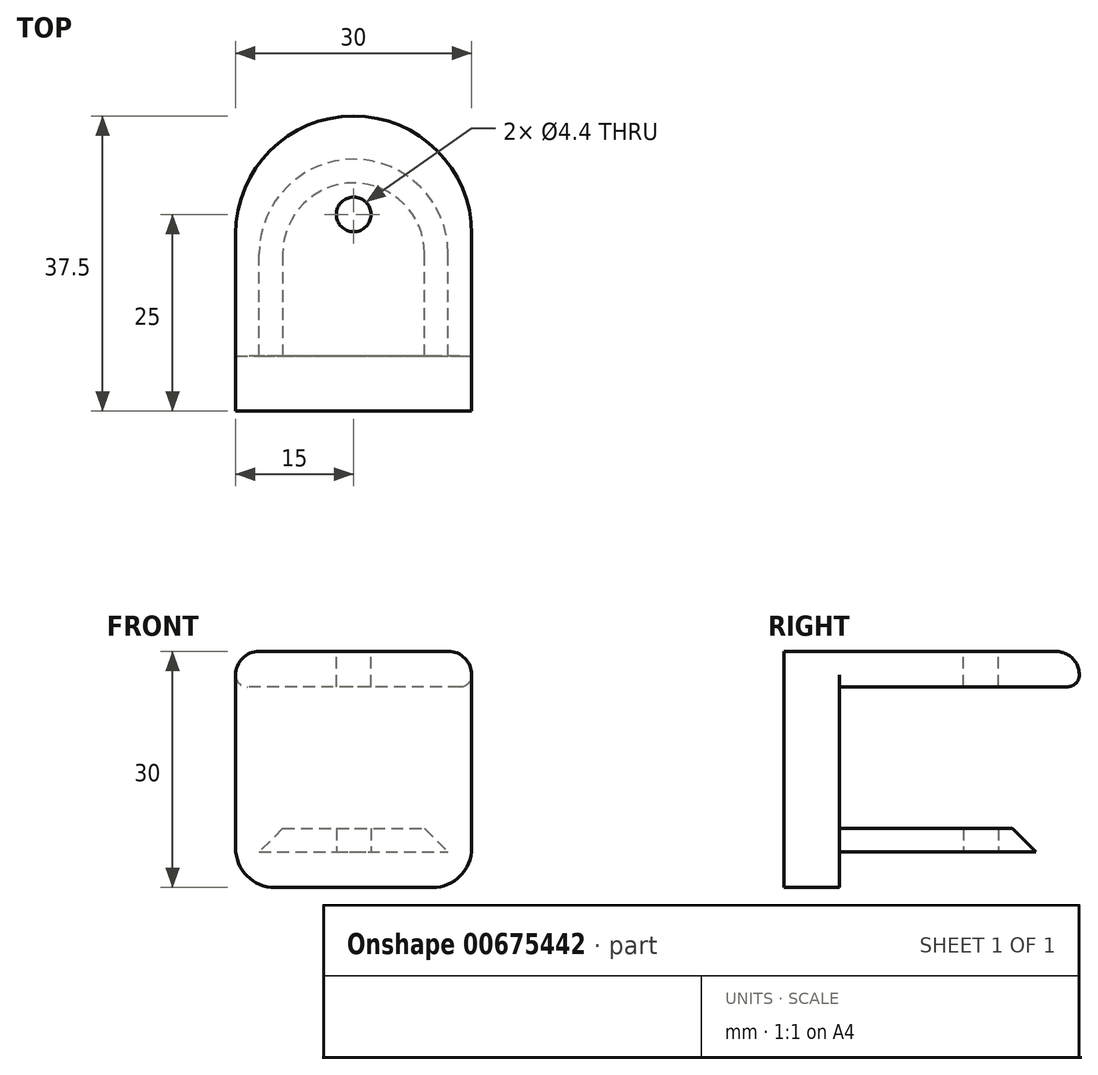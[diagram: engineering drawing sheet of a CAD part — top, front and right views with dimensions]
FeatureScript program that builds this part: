
annotation { "Feature Type Name" : "Feature", "Feature Type Description" : "" }
export const myFeature = defineFeature(function(context is Context, id is Id, definition is map)
    precondition{}
    {
        {
            var Q0;
            Q0=qCreatedBy(makeId("Front.planeOp"),FACE);
            var sketch = newSketch(context, id + "F0", { "sketchPlane" : qUnion([Q0])});
            skLineSegment(sketch, "E0.bottom", {"start": v(15, 15) * mm, "end": v(-15, 15) * mm});
            skLineSegment(sketch, "E0.top", {"start": v(10, -15) * mm, "end": v(-10, -15) * mm});
            skLineSegment(sketch, "E0.left", {"start": v(15, 15) * mm, "end": v(15, -10) * mm});
            skLineSegment(sketch, "E0.right", {"start": v(-15, 15) * mm, "end": v(-15, -10) * mm});
            skPoint(sketch, "E0.middle", {"position": v(0, 0) * mm});
            skPoint(sketch, "E1.visualSharp", {"position": v(-15, -15) * mm});
            skArc(sketch, "E1.filletArc", {"start": v(-15, -10) * mm, "mid": v(-13.54, -13.54) * mm, "end": v(-10, -15) * mm});
            skPoint(sketch, "E2.visualSharp", {"position": v(15, -15) * mm});
            skArc(sketch, "E2.filletArc", {"start": v(10, -15) * mm, "mid": v(13.54, -13.54) * mm, "end": v(15, -10) * mm});
            skPoint(sketch, "E3.visualSharp", {"position": v(15, 15) * mm});
            skPoint(sketch, "E4.visualSharp", {"position": v(-15, 15) * mm});
            skSolve(sketch);
        }
        {
            var Q0;
            Q0=makeQuery(id+"F0.imprint","IMPRINT",FACE,{"disambiguationData":[TD([[makeQuery(id+"F0.imprint","IMPRINT",EDGE,{"derivedFrom":sQuery(id+"F0.wireOp",EDGE,"E0.bottom")}),1.0]])]});
            extrude(context, id + "F1", {"entities" : qUnion([Q0]), "depth" : 7 * mm, "offsetDistance" : 25 * mm});
        }
        {
            var Q0;
            Q0=makeQuery(id+"F1.opExtrude","SWEPT_FACE",FACE,{"disambiguationData":[OSD([sQuery(id+"F0.wireOp",EDGE,"E0.bottom")])]});
            var sketch = newSketch(context, id + "F2", { "sketchPlane" : qUnion([Q0])});
            skLineSegment(sketch, "E5.0", {"start": v(-15, -7) * mm, "end": v(-15, 0) * mm});
            skPoint(sketch, "E6.0", {"position": v(15, -3.5) * mm});
            skLineSegment(sketch, "E7.0", {"start": v(15, -7) * mm, "end": v(15, 0) * mm});
            skLineSegment(sketch, "E8.bottom", {"start": v(-15, -7) * mm, "end": v(15, -7) * mm});
            skLineSegment(sketch, "E8.top", {"start": v(0, 30.5) * mm, "end": v(0, 30.5) * mm});
            skLineSegment(sketch, "E8.left", {"start": v(-15, -7) * mm, "end": v(-15, 15.5) * mm});
            skLineSegment(sketch, "E8.right", {"start": v(15, -7) * mm, "end": v(15, 15.5) * mm});
            skPoint(sketch, "E9.visualSharp", {"position": v(-15, 30.5) * mm});
            skArc(sketch, "E9.filletArc", {"start": v(0, 30.5) * mm, "mid": v(-10.6, 26.1) * mm, "end": v(-15, 15.5) * mm});
            skPoint(sketch, "E10.visualSharp", {"position": v(15, 30.5) * mm});
            skArc(sketch, "E10.filletArc", {"start": v(15, 15.5) * mm, "mid": v(10.6, 26.1) * mm, "end": v(0, 30.5) * mm});
            skSolve(sketch);
        }
        {
            var Q0;
            Q0 = qSketchRegion(id + "F2", true);
            extrude(context, id + "F3", {"entities" : qUnion([Q0]), "operationType" : NewBodyOperationType.ADD, "oppositeDirection" : true, "depth" : 4.5 * mm, "offsetDistance" : 25 * mm});
        }
        {
            var Q0;
            Q0=makeQuery(id+"F3.boolean.opBoolean","MERGE",EDGE,{"derivedFrom":[makeQuery(id+"F1.opExtrude","SWEPT_EDGE",EDGE,{"disambiguationData":[OSD([sQuery(id+"F0.wireOp",EDGE,"E0.bottom"),sQuery(id+"F0.wireOp",EDGE,"E0.left")])]}),makeQuery(id+"F3.opExtrude","CAP_EDGE",EDGE,{"disambiguationData":[OSD([sQuery(id+"F2.wireOp",EDGE,"E8.right")])],"isStart":true})]});
            fillet(context, id + "F4", {"entities" : qUnion([Q0]), "radius" : 3 * mm, "tangentPropagation" : true, "allowEdgeOverflow" : false});
        }
        {
            var Q0;
            Q0=makeQuery(id+"F3.opExtrude","CAP_EDGE",EDGE,{"disambiguationData":[OSD([sQuery(id+"F2.wireOp",EDGE,"E8.right")])],"isStart":false});
            fillet(context, id + "F5", {"entities" : qUnion([Q0]), "radius" : 1.5 * mm, "tangentPropagation" : true, "allowEdgeOverflow" : false});
        }
        {
            var Q0;
            Q0=makeQuery(id+"F3.boolean.opBoolean","MERGE",FACE,{"derivedFrom":[makeQuery(id+"F1.opExtrude","SWEPT_FACE",FACE,{"disambiguationData":[OSD([sQuery(id+"F0.wireOp",EDGE,"E0.bottom")])]}),makeQuery(id+"F3.opExtrude","CAP_FACE",FACE,{"disambiguationData":[OSD([sQuery(id+"F2.wireOp",EDGE,"E8.bottom"),sQuery(id+"F2.wireOp",EDGE,"E8.left"),sQuery(id+"F2.wireOp",EDGE,"E8.right"),sQuery(id+"F2.wireOp",EDGE,"E9.filletArc"),sQuery(id+"F2.wireOp",EDGE,"E10.filletArc")])],"isStart":true})]});
            var sketch = newSketch(context, id + "F6", { "sketchPlane" : qUnion([Q0])});
            skPoint(sketch, "E11", {"position": v(0, 18) * mm});
            skSolve(sketch);
        }
        {
            var Q0;
            Q0=sQuery(id+"F6.wireOp",VERTEX,"E11");
            var Q1;
            Q1=makeQuery(id+"F1.opExtrude","SWEPT_BODY",BODY,{"disambiguationData":[OSD([sQuery(id+"F0.wireOp",EDGE,"E0.bottom"),sQuery(id+"F0.wireOp",EDGE,"E0.top"),sQuery(id+"F0.wireOp",EDGE,"E0.left"),sQuery(id+"F0.wireOp",EDGE,"E0.right"),sQuery(id+"F0.wireOp",EDGE,"E1.filletArc"),sQuery(id+"F0.wireOp",EDGE,"E2.filletArc")])]});
            hole(context, id + "F7", {"style" : HoleStyle.SIMPLE, "endStyle" : HoleEndStyle.THROUGH, "standardTappedOrClearance" : lookupTablePath({ "standard" : "ISO", "fit" : "Normal", "size" : "M4", "type" : "Clearance" }), "standardBlindInLast" : lookupTablePath({ "fit" : "Standard", "standard" : "ISO", "size" : "M4", "type" : "Clearance" }), "holeDiameter" : 4.4 * mm, "majorDiameter" : 5 * mm, "isTappedThrough" : true, "tappedDepth" : 12 * mm, "tapClearance" : 3, "locations" : qUnion([Q0]), "scope" : qUnion([Q1])});
        }
        {
            var Q0;
            Q0=makeQuery(id+"F1.opExtrude","SWEPT_FACE",FACE,{"disambiguationData":[OSD([sQuery(id+"F0.wireOp",EDGE,"E0.top")])]});
            cPlane(context, id + "F8", {"entities" : qUnion([Q0]), "cplaneType" : CPlaneType.OFFSET, "offset" : 4.5 * mm, "oppositeDirection" : true, "width" : 150 * mm, "height" : 150 * mm});
        }
        {
            var Q0;
            Q0=qCreatedBy(id+"F8.planeOp",FACE);
            var sketch = newSketch(context, id + "F9", { "sketchPlane" : qUnion([Q0])});
            skLineSegment(sketch, "E12.bottom", {"start": v(-12, 0) * mm, "end": v(12, 0) * mm});
            skLineSegment(sketch, "E12.top", {"start": v(0, -25) * mm, "end": v(0, -25) * mm});
            skLineSegment(sketch, "E12.left", {"start": v(-12, 0) * mm, "end": v(-12, -13) * mm});
            skLineSegment(sketch, "E12.right", {"start": v(12, 0) * mm, "end": v(12, -13) * mm});
            skPoint(sketch, "E13.visualSharp", {"position": v(-12, -25) * mm});
            skArc(sketch, "E13.filletArc", {"start": v(-12, -13) * mm, "mid": v(-8.49, -21.49) * mm, "end": v(0, -25) * mm});
            skPoint(sketch, "E14.visualSharp", {"position": v(12, -25) * mm});
            skArc(sketch, "E14.filletArc", {"start": v(0, -25) * mm, "mid": v(8.49, -21.49) * mm, "end": v(12, -13) * mm});
            skSolve(sketch);
        }
        {
            var Q0;
            Q0=makeQuery(id+"F9.imprint","IMPRINT",FACE,{"disambiguationData":[TD([[makeQuery(id+"F9.imprint","IMPRINT",EDGE,{"derivedFrom":sQuery(id+"F9.wireOp",EDGE,"E12.bottom")}),-1.0]])]});
            extrude(context, id + "F10", {"entities" : qUnion([Q0]), "operationType" : NewBodyOperationType.ADD, "oppositeDirection" : true, "depth" : 3 * mm, "offsetDistance" : 25 * mm});
        }
        {
            var Q0;
            Q0=makeQuery(id+"F10.opExtrude","CAP_FACE",FACE,{"disambiguationData":[OSD([sQuery(id+"F9.wireOp",EDGE,"E12.bottom"),sQuery(id+"F9.wireOp",EDGE,"E12.left"),sQuery(id+"F9.wireOp",EDGE,"E12.right"),sQuery(id+"F9.wireOp",EDGE,"E13.filletArc"),sQuery(id+"F9.wireOp",EDGE,"E14.filletArc")])],"isStart":true});
            var sketch = newSketch(context, id + "F11", { "sketchPlane" : qUnion([Q0])});
            skCircle(sketch, "E15.0", {"center": v(0, -18) * mm, "radius": 2.2 * mm});
            skSolve(sketch);
        }
        {
            var Q0;
            Q0=makeQuery(id+"F11.imprint","IMPRINT",FACE,{"disambiguationData":[TD([[makeQuery(id+"F11.imprint","IMPRINT",EDGE,{"derivedFrom":sQuery(id+"F11.wireOp",EDGE,"E15.0")}),1.0]])]});
            extrude(context, id + "F12", {"entities" : qUnion([Q0]), "operationType" : NewBodyOperationType.REMOVE, "oppositeDirection" : true, "depth" : 3 * mm, "offsetDistance" : 25 * mm});
        }
        {
            var Q0;
            Q0=makeQuery(id+"F10.opExtrude","CAP_EDGE",EDGE,{"disambiguationData":[OSD([sQuery(id+"F9.wireOp",EDGE,"E12.left")])],"isStart":false});
            chamfer(context, id + "F13", {"entities" : qUnion([Q0]), "width" : 3 * mm, "tangentPropagation" : true});
        }
    });
